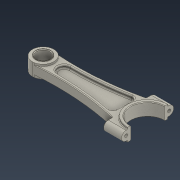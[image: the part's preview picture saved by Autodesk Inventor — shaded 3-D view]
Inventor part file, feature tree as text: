
AUTODESK INVENTOR PART (.ipt)
format: ipt  version: 2022 (Build 260153000, 153)  size: 297,984 bytes
history: native  units: mm
features: extrude x4, sketch x3, fillet x2, other x2, chamfer x2, hole x1, mirror x1
ambient origin geometry x8: Origin, YZ Plane, XZ Plane, XY Plane, X Axis, Y Axis, Z Axis, Center Point
bodies: Solid1 (feature_tree)
feature tree (15):
  sketch  "Sketch1"  dims[d0=170.0mm d1=22.0mm]
  extrude  "Extrusion1"  Depth=22.0mm
  extrude  "Extrusion2"  Depth=121.0mm
  extrude  "Extrusion3"  Depth=10.0mm
  extrude  "Extrusion4"  Depth=10.0mm
  hole  "Hole1"  [1 undecoded]
  mirror  "Mirror1"
  fillet  "Fillet1"  Radius=10.0mm
  other  "Full Round Fillet1"
  other  "Full Round Fillet2"
  chamfer  "Chamfer1"  Distance=15.0mm
  fillet  "Fillet3"  Radius=450.0mm
  chamfer  "Chamfer2"  Distance=21.0mm
  sketch  "Sketch2"  dims[d2=55.0mm d3=121.0mm]
  sketch  "Sketch3"  dims[d4=25.0mm d5=35.0mm d7=65.0mm d8=30.0mm d9=10.0mm d10=15.0mm d11=450.0mm d12=21.0mm d13=0.0mm d14=15.0mm d15=0.0mm d16=23.0mm d17=0.0mm d18=6.0mm d19=15.0mm d20=83.0mm d21=5.0mm d22=5.0mm d23=0.0mm d24=2.0mm d25=5.0mm d26=17.0mm d27=4.0mm d28=2.0mm d29=90.0deg d30=17.0mm d31=20.594885mm d33=1.0mm d34=2.0mm d35=45.0deg d36=1.0mm d37=1.0mm d38=2.0mm d39=45.0deg d32=0.75mm]
note: 1 required parameter value undecoded (feature->parameter linkage not recoverable at this tier; creation-order binding heuristic only, values carry confidence <= 0.55)
